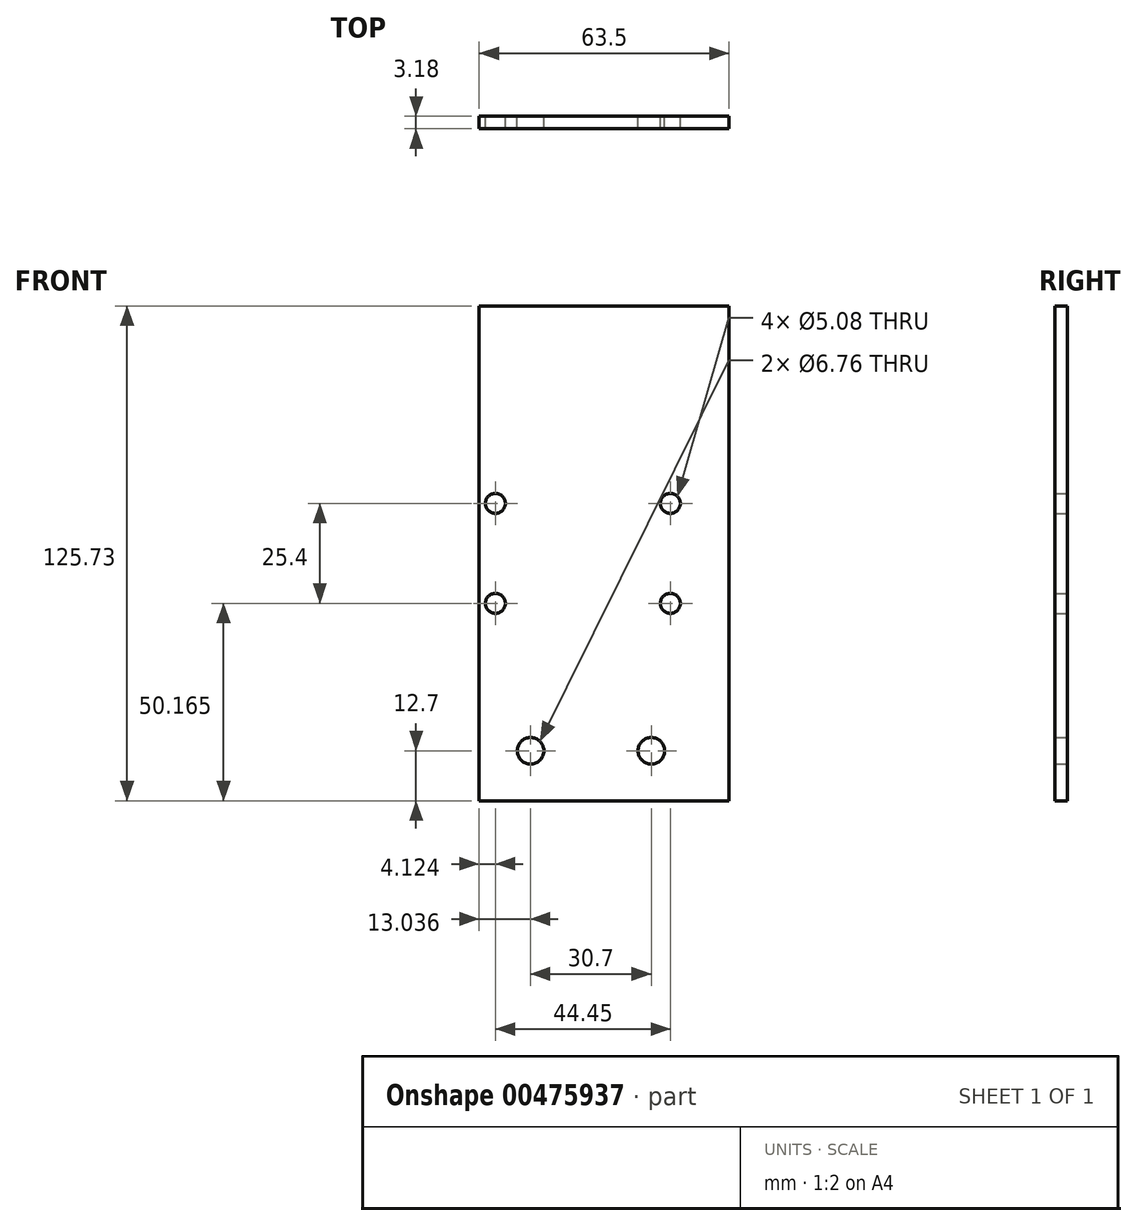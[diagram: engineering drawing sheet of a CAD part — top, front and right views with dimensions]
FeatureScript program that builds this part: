
annotation { "Feature Type Name" : "Feature", "Feature Type Description" : "" }
export const myFeature = defineFeature(function(context is Context, id is Id, definition is map)
    precondition{}
    {
        {
            var Q0;
            Q0=qCreatedBy(makeId("Front.planeOp"),FACE);
            var sketch = newSketch(context, id + "F0", { "sketchPlane" : qUnion([Q0])});
            skLineSegment(sketch, "E0.bottom", {"start": v(-30.02, 113.03) * mm, "end": v(33.48, 113.03) * mm});
            skLineSegment(sketch, "E0.top", {"start": v(-30.02, -12.7) * mm, "end": v(33.48, -12.7) * mm});
            skLineSegment(sketch, "E0.left", {"start": v(-30.02, 113.03) * mm, "end": v(-30.02, -12.7) * mm});
            skLineSegment(sketch, "E0.right", {"start": v(33.48, 113.03) * mm, "end": v(33.48, -12.7) * mm});
            skCircle(sketch, "E1", {"center": v(-25.9, 62.87) * mm, "radius": 2.54 * mm});
            skCircle(sketch, "E2", {"center": v(-25.9, 37.47) * mm, "radius": 2.54 * mm});
            skCircle(sketch, "E3", {"center": v(18.55, 62.87) * mm, "radius": 2.54 * mm});
            skCircle(sketch, "E4", {"center": v(18.55, 37.47) * mm, "radius": 2.54 * mm});
            skCircle(sketch, "E5", {"center": v(-16.98, 0) * mm, "radius": 3.38 * mm});
            skCircle(sketch, "E6", {"center": v(13.72, 0) * mm, "radius": 3.38 * mm});
            skSolve(sketch);
        }
        {
            var Q0;
            Q0=makeQuery(id+"F0.imprint","IMPRINT",FACE,{"disambiguationData":[TD([[makeQuery(id+"F0.imprint","IMPRINT",EDGE,{"derivedFrom":sQuery(id+"F0.wireOp",EDGE,"E0.bottom")}),-1.0]])]});
            extrude(context, id + "F1", {"entities" : qUnion([Q0]), "depth" : 3.17 * mm});
        }
    });
